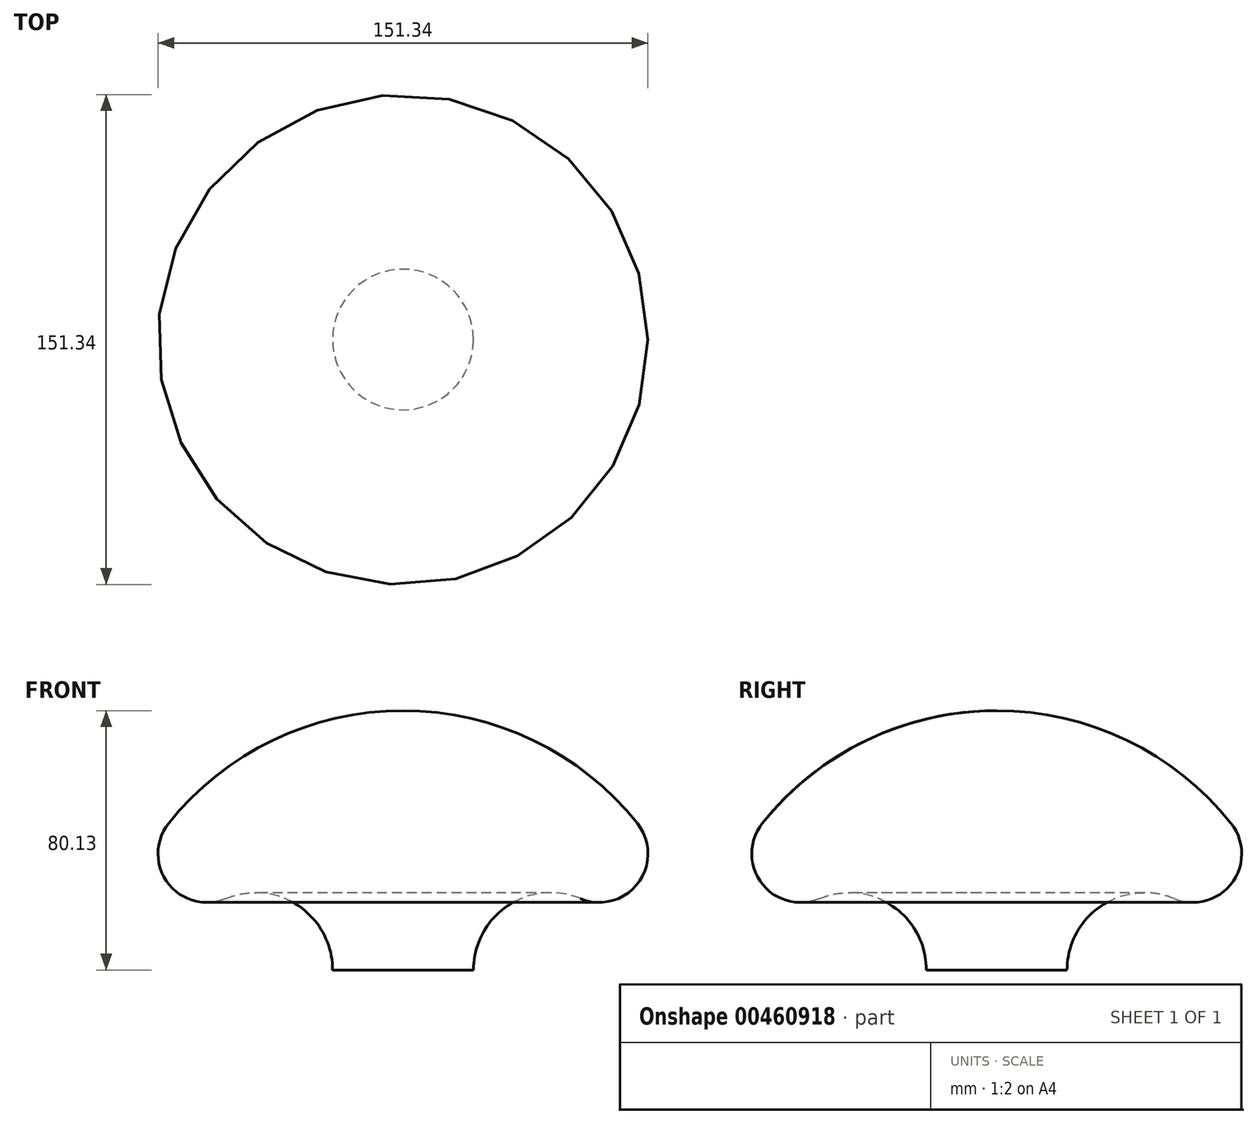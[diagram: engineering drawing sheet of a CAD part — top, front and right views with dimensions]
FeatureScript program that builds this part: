
annotation { "Feature Type Name" : "Feature", "Feature Type Description" : "" }
export const myFeature = defineFeature(function(context is Context, id is Id, definition is map)
    precondition{}
    {
        {
            var Q0;
            Q0=qCreatedBy(makeId("Right.planeOp"),FACE);
            var sketch = newSketch(context, id + "F0", { "sketchPlane" : qUnion([Q0])});
            skLineSegment(sketch, "E0", {"start": v(0, 61.36) * mm, "end": v(0, -53.83) * mm, "construction": true});
            skLineSegment(sketch, "E1", {"start": v(0, -46.78) * mm, "end": v(-21.73, -46.78) * mm});
            skLineSegment(sketch, "E2", {"start": v(-21.73, -46.78) * mm, "end": v(-21.73, -53.25) * mm, "construction": true});
            skArc(sketch, "E3", {"start": v(-21.73, -46.78) * mm, "mid": v(-32.38, -26.9) * mm, "end": v(-54.83, -24.74) * mm});
            skArc(sketch, "E4", {"start": v(-54.83, -24.74) * mm, "mid": v(-72.63, -19.93) * mm, "end": v(-72.38, -1.48) * mm});
            skLineSegment(sketch, "E5", {"start": v(-6.23, 33.35) * mm, "end": v(0, 33.35) * mm, "construction": true});
            skArc(sketch, "E6", {"start": v(-72.38, -1.48) * mm, "mid": v(-40.16, 24.2) * mm, "end": v(0, 33.35) * mm});
            skLineSegment(sketch, "E7", {"start": v(0, 33.35) * mm, "end": v(0, -46.78) * mm});
            skSolve(sketch);
        }
        {
            var Q0;
            Q0 = qSketchRegion(id + "F0", true);
            var Q1;
            Q1=sQuery(id+"F0.wireOp",EDGE,"E0");
            revolve(context, id + "F1", {"surfaceOperationType" : NewSurfaceOperationType.NEW, "entities" : qUnion([Q0]), "axis" : qUnion([Q1]), "revolveType" : RevolveType.FULL});
        }
    });
